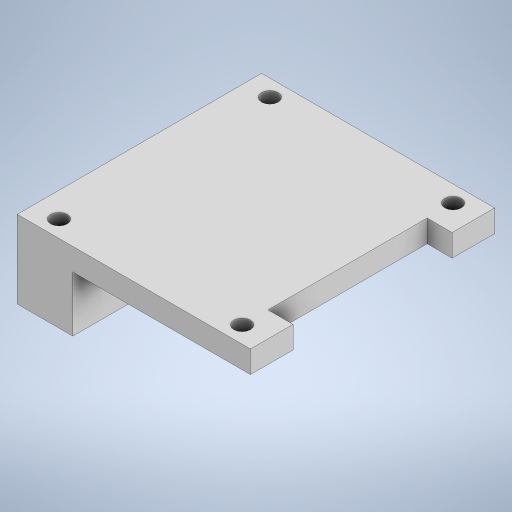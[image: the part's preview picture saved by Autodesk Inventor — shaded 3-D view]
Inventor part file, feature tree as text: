
AUTODESK INVENTOR PART (.ipt)
format: ipt  version: 2024.2 (Build 282272000, 272)  size: 227,840 bytes
history: native  units: mm
features: extrude x2, sketch x2, other x1
ambient origin geometry x8: Origin, YZ Plane, XZ Plane, XY Plane, X Axis, Y Axis, Z Axis, Center Point
bodies: Body1 (feature_tree)
feature tree (5):
  other  "Твердое тело1"
  extrude  "Выдавливание1"  Depth=38.0mm
  extrude  "Выдавливание2"  Depth=33.0mm
  sketch  "Эскиз1"
  sketch  "Эскиз2"
